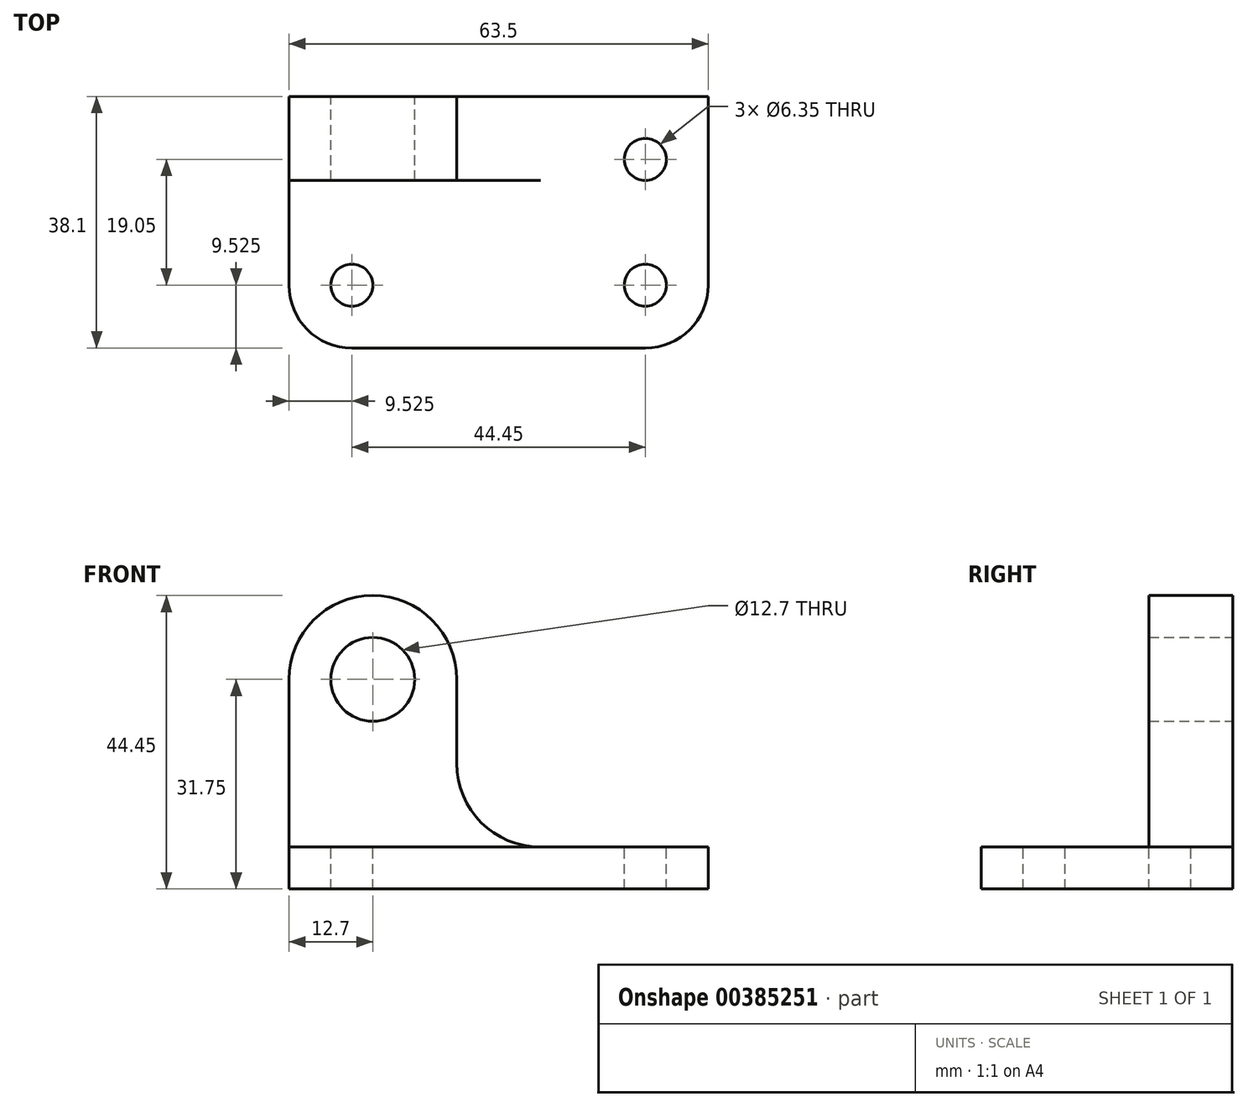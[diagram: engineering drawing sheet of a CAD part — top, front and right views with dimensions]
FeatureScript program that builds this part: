
annotation { "Feature Type Name" : "Feature", "Feature Type Description" : "" }
export const myFeature = defineFeature(function(context is Context, id is Id, definition is map)
    precondition{}
    {
        {
            var Q0;
            Q0=qCreatedBy(makeId("Right.planeOp"),FACE);
            var sketch = newSketch(context, id + "F0", { "sketchPlane" : qUnion([Q0])});
            skLineSegment(sketch, "E0", {"start": v(0, 0) * mm, "end": v(38.1, 0) * mm});
            skLineSegment(sketch, "E1", {"start": v(38.1, 0) * mm, "end": v(38.1, 44.45) * mm});
            skLineSegment(sketch, "E2", {"start": v(38.1, 44.45) * mm, "end": v(0, 44.45) * mm});
            skLineSegment(sketch, "E3", {"start": v(0, 44.45) * mm, "end": v(0, 0) * mm});
            skSolve(sketch);
        }
        {
            var Q0;
            Q0=qSketchRegion(id+"F0",true);
            extrude(context, id + "F1", {"entities" : qUnion([Q0]), "depth" : 63.5 * mm});
        }
        {
            var Q0;
            Q0=makeQuery(id+"F1.opExtrude","SWEPT_FACE",FACE,{"disambiguationData":[OSD([sQuery(id+"F0.wireOp",EDGE,"E1")])]});
            var sketch = newSketch(context, id + "F2", { "sketchPlane" : qUnion([Q0])});
            skLineSegment(sketch, "E4", {"start": v(0, 6.35) * mm, "end": v(-25.4, 6.35) * mm});
            skArc(sketch, "E5", {"start": v(-38.1, 31.75) * mm, "mid": v(-50.8, 44.45) * mm, "end": v(-63.5, 31.75) * mm});
            skArc(sketch, "E6", {"start": v(-38.1, 19.05) * mm, "mid": v(-34.38, 10.07) * mm, "end": v(-25.4, 6.35) * mm});
            skLineSegment(sketch, "E7", {"start": v(-38.1, 31.75) * mm, "end": v(-38.1, 19.05) * mm});
            skCircle(sketch, "E8", {"center": v(-50.8, 31.75) * mm, "radius": 6.35 * mm});
            skSolve(sketch);
        }
        {
            var Q0;
            Q0=qSketchRegion(id+"F2",true);
            var Q1;
            {var subQ5=sQuery(id+"F2.wireOp",EDGE,"E4");Q1=makeQuery(id+"F2.imprint","IMPRINT",FACE,{"disambiguationData":[TD([[makeQuery(id+"F2.imprint","IMPRINT",EDGE,{"derivedFrom":subQ5}),-1.0]])]});}
            var Q2;
            {var subQ0=sQuery(id+"F2.wireOp",EDGE,"E5");var subQ1=sQuery(id+"F0.wireOp",EDGE,"E1");var subQ2=makeQuery(id+"F1.opExtrude","CAP_EDGE",EDGE,{"disambiguationData":[OSD([subQ1])],"isStart":false});var subQ3=makeQuery(id+"F2.imprint","INTERSECT",VERTEX,{"derivedFrom":[subQ2,subQ0]});Q2=makeQuery(id+"F2.imprint","IMPRINT",FACE,{"disambiguationData":[TD([[makeQuery(id+"F2.imprint","IMPRINT",EDGE,{"disambiguationData":[TD([[subQ3,1.0]])],"derivedFrom":subQ0}),-1.0]])]});}
            extrude(context, id + "F3", {"entities" : qUnion([Q0, Q1, Q2]), "operationType" : NewBodyOperationType.REMOVE, "oppositeDirection" : true, "depth" : 76.2 * mm});
        }
        {
            var Q0;
            Q0=makeQuery(id+"F1.opExtrude","CAP_FACE",FACE,{"disambiguationData":[OSD([sQuery(id+"F0.wireOp",EDGE,"E0"),sQuery(id+"F0.wireOp",EDGE,"E1"),sQuery(id+"F0.wireOp",EDGE,"E2"),sQuery(id+"F0.wireOp",EDGE,"E3")])],"isStart":false});
            var sketch = newSketch(context, id + "F4", { "sketchPlane" : qUnion([Q0])});
            skLineSegment(sketch, "E9", {"start": v(25.4, 31.75) * mm, "end": v(25.4, 6.35) * mm});
            skLineSegment(sketch, "E10", {"start": v(25.4, 6.35) * mm, "end": v(0, 6.35) * mm});
            skSolve(sketch);
        }
        {
            var Q0;
            {var subQ0=sQuery(id+"F4.wireOp",EDGE,"E9");Q0=makeQuery(id+"F4.imprint","IMPRINT",FACE,{"disambiguationData":[TD([[makeQuery(id+"F4.imprint","IMPRINT",EDGE,{"derivedFrom":subQ0}),-1.0]])]});}
            extrude(context, id + "F5", {"entities" : qUnion([Q0]), "operationType" : NewBodyOperationType.REMOVE, "oppositeDirection" : true, "depth" : 76.2 * mm});
        }
        {
            var Q0;
            Q0=makeQuery(id+"F5.boolean.opBoolean","MERGE",FACE,{"derivedFrom":[makeQuery(id+"F3.boolean.opBoolean","COPY",FACE,{"derivedFrom":makeQuery(id+"F3.opExtrude","SWEPT_FACE",FACE,{"disambiguationData":[OSD([sQuery(id+"F2.wireOp",EDGE,"E4")])]})}),makeQuery(id+"F5.opExtrude","SWEPT_FACE",FACE,{"disambiguationData":[OSD([sQuery(id+"F4.wireOp",EDGE,"E10")])]})]});
            extrude(context, id + "F6", {"entities" : qUnion([Q0]), "operationType" : NewBodyOperationType.ADD, "depth" : 50.8 * mm});
        }
        {
            var Q0;
            {var subQ0=sQuery(id+"F0.wireOp",EDGE,"E1");Q0=makeQuery(id+"F6.boolean.opBoolean","MERGE",FACE,{"derivedFrom":[makeQuery(id+"F1.opExtrude","CAP_FACE",FACE,{"disambiguationData":[OSD([sQuery(id+"F0.wireOp",EDGE,"E0"),subQ0,sQuery(id+"F0.wireOp",EDGE,"E2"),sQuery(id+"F0.wireOp",EDGE,"E3")])],"isStart":true}),makeQuery(id+"F6.opExtrude","SWEPT_FACE",FACE,{"disambiguationData":[OSD([subQ0,sQuery(id+"F2.wireOp",EDGE,"E4")])]})]});}
            var sketch = newSketch(context, id + "F7", { "sketchPlane" : qUnion([Q0])});
            skLineSegment(sketch, "E11", {"start": v(-38.1, 6.35) * mm, "end": v(0, 6.35) * mm});
            skSolve(sketch);
        }
        {
            var Q0;
            {var subQ0=sQuery(id+"F7.wireOp",EDGE,"E11");Q0=makeQuery(id+"F7.imprint","IMPRINT",FACE,{"disambiguationData":[TD([[makeQuery(id+"F7.imprint","IMPRINT",EDGE,{"derivedFrom":subQ0}),1.0]])]});}
            extrude(context, id + "F8", {"entities" : qUnion([Q0]), "operationType" : NewBodyOperationType.REMOVE, "oppositeDirection" : true, "depth" : 25.4 * mm});
        }
        {
            var Q0;
            Q0=makeQuery(id+"F6.boolean.opBoolean","MERGE",FACE,{"derivedFrom":[makeQuery(id+"F1.opExtrude","CAP_FACE",FACE,{"disambiguationData":[OSD([sQuery(id+"F0.wireOp",EDGE,"E0"),sQuery(id+"F0.wireOp",EDGE,"E1"),sQuery(id+"F0.wireOp",EDGE,"E2"),sQuery(id+"F0.wireOp",EDGE,"E3")])],"isStart":false}),makeQuery(id+"F6.opExtrude","SWEPT_FACE",FACE,{"disambiguationData":[OSD([sQuery(id+"F4.wireOp",EDGE,"E10")])]})]});
            var sketch = newSketch(context, id + "F9", { "sketchPlane" : qUnion([Q0])});
            skLineSegment(sketch, "E12", {"start": v(25.4, 31.75) * mm, "end": v(25.4, 6.35) * mm});
            skLineSegment(sketch, "E13", {"start": v(25.4, 6.35) * mm, "end": v(0, 6.35) * mm});
            skSolve(sketch);
        }
        {
            var Q0;
            Q0=makeQuery(id+"F9.imprint","IMPRINT",FACE,{"disambiguationData":[TD([[makeQuery(id+"F9.imprint","IMPRINT",EDGE,{"derivedFrom":sQuery(id+"F9.wireOp",EDGE,"E12")}),-1.0]])]});
            extrude(context, id + "F10", {"entities" : qUnion([Q0]), "operationType" : NewBodyOperationType.REMOVE, "oppositeDirection" : true, "depth" : 76.2 * mm, "hasDraft" : true, "draftAngle" : 0 * degree});
        }
        {
            var Q0;
            Q0=makeQuery(id+"F10.boolean.opBoolean","MERGE",FACE,{"derivedFrom":[makeQuery(id+"F8.boolean.opBoolean","COPY",FACE,{"derivedFrom":makeQuery(id+"F8.opExtrude","SWEPT_FACE",FACE,{"disambiguationData":[OSD([sQuery(id+"F7.wireOp",EDGE,"E11")])]})}),makeQuery(id+"F10.opExtrude","SWEPT_FACE",FACE,{"disambiguationData":[OSD([sQuery(id+"F9.wireOp",EDGE,"E13")])]})]});
            var sketch = newSketch(context, id + "F11", { "sketchPlane" : qUnion([Q0])});
            skArc(sketch, "E14", {"start": v(0, 9.52) * mm, "mid": v(2.79, 2.79) * mm, "end": v(9.53, 0) * mm});
            skCircle(sketch, "E15", {"center": v(9.53, 9.52) * mm, "radius": 3.18 * mm});
            skCircle(sketch, "E16", {"center": v(53.98, 9.53) * mm, "radius": 3.18 * mm});
            skCircle(sketch, "E17", {"center": v(9.52, 28.58) * mm, "radius": 3.18 * mm});
            skArc(sketch, "E18", {"start": v(53.98, 0) * mm, "mid": v(60.71, 2.79) * mm, "end": v(63.5, 9.53) * mm});
            skSolve(sketch);
        }
        {
            var Q0;
            {var subQ0=sQuery(id+"F11.wireOp",EDGE,"E14");Q0=makeQuery(id+"F11.imprint","IMPRINT",FACE,{"disambiguationData":[TD([[makeQuery(id+"F11.imprint","IMPRINT",EDGE,{"derivedFrom":subQ0}),-1.0]])]});}
            var Q1;
            Q1=makeQuery(id+"F11.imprint","IMPRINT",FACE,{"disambiguationData":[TD([[makeQuery(id+"F11.imprint","IMPRINT",EDGE,{"derivedFrom":sQuery(id+"F11.wireOp",EDGE,"E15")}),1.0]])]});
            var Q2;
            Q2=makeQuery(id+"F11.imprint","IMPRINT",FACE,{"disambiguationData":[TD([[makeQuery(id+"F11.imprint","IMPRINT",EDGE,{"derivedFrom":sQuery(id+"F11.wireOp",EDGE,"E16")}),1.0]])]});
            var Q3;
            {var subQ0=sQuery(id+"F11.wireOp",EDGE,"KBLp3CoG-kTUa-TUTr-mOAm-0BXdPAIyydLt");Q3=makeQuery(id+"F11.imprint","IMPRINT",FACE,{"disambiguationData":[TD([[makeQuery(id+"F11.imprint","IMPRINT",EDGE,{"derivedFrom":subQ0}),-1.0]])]});}
            var Q4;
            Q4=makeQuery(id+"F11.imprint","IMPRINT",FACE,{"disambiguationData":[TD([[makeQuery(id+"F11.imprint","IMPRINT",EDGE,{"derivedFrom":sQuery(id+"F11.wireOp",EDGE,"E17")}),1.0]])]});
            var Q5;
            {var subQ0=sQuery(id+"F11.wireOp",EDGE,"E18");Q5=makeQuery(id+"F11.imprint","IMPRINT",FACE,{"disambiguationData":[TD([[makeQuery(id+"F11.imprint","IMPRINT",EDGE,{"derivedFrom":subQ0}),-1.0]])]});}
            extrude(context, id + "F12", {"entities" : qUnion([Q0, Q1, Q2, Q3, Q4, Q5]), "operationType" : NewBodyOperationType.REMOVE, "oppositeDirection" : true, "depth" : 25.4 * mm});
        }
        {
            var Q0;
            Q0=makeQuery(id+"F1.opExtrude","SWEPT_BODY",BODY,{"disambiguationData":[OSD([sQuery(id+"F0.wireOp",EDGE,"E0"),sQuery(id+"F0.wireOp",EDGE,"E1"),sQuery(id+"F0.wireOp",EDGE,"E2"),sQuery(id+"F0.wireOp",EDGE,"E3")])]});
            var Q1;
            Q1=qCreatedBy(makeId("Right.planeOp"),FACE);
            mirror(context, id + "F13", {"entities" : qUnion([Q0]), "mirrorPlane" : qUnion([Q1])});
        }
        {
            var Q0;
            Q0=makeQuery(id+"F13.opPattern","COPY",BODY,{"derivedFrom":makeQuery(id+"F1.opExtrude","SWEPT_BODY",BODY,{"disambiguationData":[OSD([sQuery(id+"F0.wireOp",EDGE,"E0"),sQuery(id+"F0.wireOp",EDGE,"E1"),sQuery(id+"F0.wireOp",EDGE,"E2"),sQuery(id+"F0.wireOp",EDGE,"E3")])]}),"instanceName":"1"});
            var Q1;
            Q1=qCreatedBy(makeId("Right.planeOp"),FACE);
            mirror(context, id + "F14", {"operationType" : NewBodyOperationType.REMOVE, "entities" : qUnion([Q0]), "mirrorPlane" : qUnion([Q1])});
        }
    });
